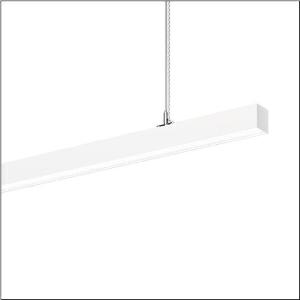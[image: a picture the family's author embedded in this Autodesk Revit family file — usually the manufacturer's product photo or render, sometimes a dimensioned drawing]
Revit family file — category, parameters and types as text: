
# Revit family: silica_r__21_51mx33tctdw_01d4
name_source: partatom
category: Lighting Fixtures
units: mm (PartAtom-declared; Revit-internal decimal feet)

## family parameters
Cut with Voids When Loaded = No
Host = Face
Light Source = No
Part Type = Normal
Room Calculation Point = No
Round Connector Dimension = Use Diameter
Shared = No

## types (1)
- --- (1 x LED, 14340 lm, 134.7 W, 6500K)
    Apparent Load = 135 VA
    CIE Flux Codes = 78 96 99 56 100
    Color Rendering = 80
    Color Temperature = 6500K
    Default Elevation = 1800 mm
    Description = Silica® 21, office luminaire, primary optical cover: prismatic diffuser, of PMMA, CAT 2 (L<= 3000cd/m²), light emission: direct/indirect distribution, primary light characteristic: symmetric, installation type: suspended mounting, LED, rated luminous flux: 14.340lm, luminous efficacy: 101lm/W, light colour: 8tw, colour temperature: 2700..6500K, control gear: ECG DALI, with terminal, 3+2-pole, max. 2.5mm², mains connection: 220..240V, AC, 50/60Hz, rated input power: 141.4W, luminaire housing, of aluminium, traffic white (RAL 9016), length: 3.004mm, width: 53mm, height: 53mm, protection rating (complete): IP20, insulation class (complete): insulation class I (protective earthing), certification: CE, permissible operating ambient temperature: 0..+35°C, standard: EN 50419, packaging unit: 1 piece
    Height = 53 mm
    Lamp = 1 x LED
    Lamp Light Flux = 14340 lm
    Lamp Power = 134.7 W
    Lamp count = 1
    Length = 3004 mm
    Luminous efficacy = 106 lm/W
    Manufacturer = Siteco
    ModVariant = No
    Model = 51MX33TCTDW
    Mounting Place = Ceiling
    Mounting Type = Pendant
    Number of Poles = 1
    OnlyDefault = Yes
    Power Factor = 1
    Product Name = Silica® 21
    Product group = office luminaire | ceiling pendant
    ProductGroupID = 902
    Protection Class = Protection class I
    Protection Degree = IP 20
    RLX_Detail_Level = 1
    RLX_Emergency_Light_Flux = 0 lm
    RLX_Emergency_Type = 0
    RLX_Emergency_Type_DB = No
    RlxData = <blob elided: 18109 chars, md5=1355c491>
    Socket = socket
    Standby Power = 0 W
    System Light Flux = 14340 lm
    System Power = 135 W
    Type Comments = individual setting
    Type Image = l_1335916.jpg
    URL = http://relux.com
    VarID = @adj_109573
    Voltage = 0 V
    Weight = 0.00 kg
    Width = 53 mm

## geometry (parser evidence)
native form markers: Blend x4, Sweep x15
no freeform markers — native parametric forms only
